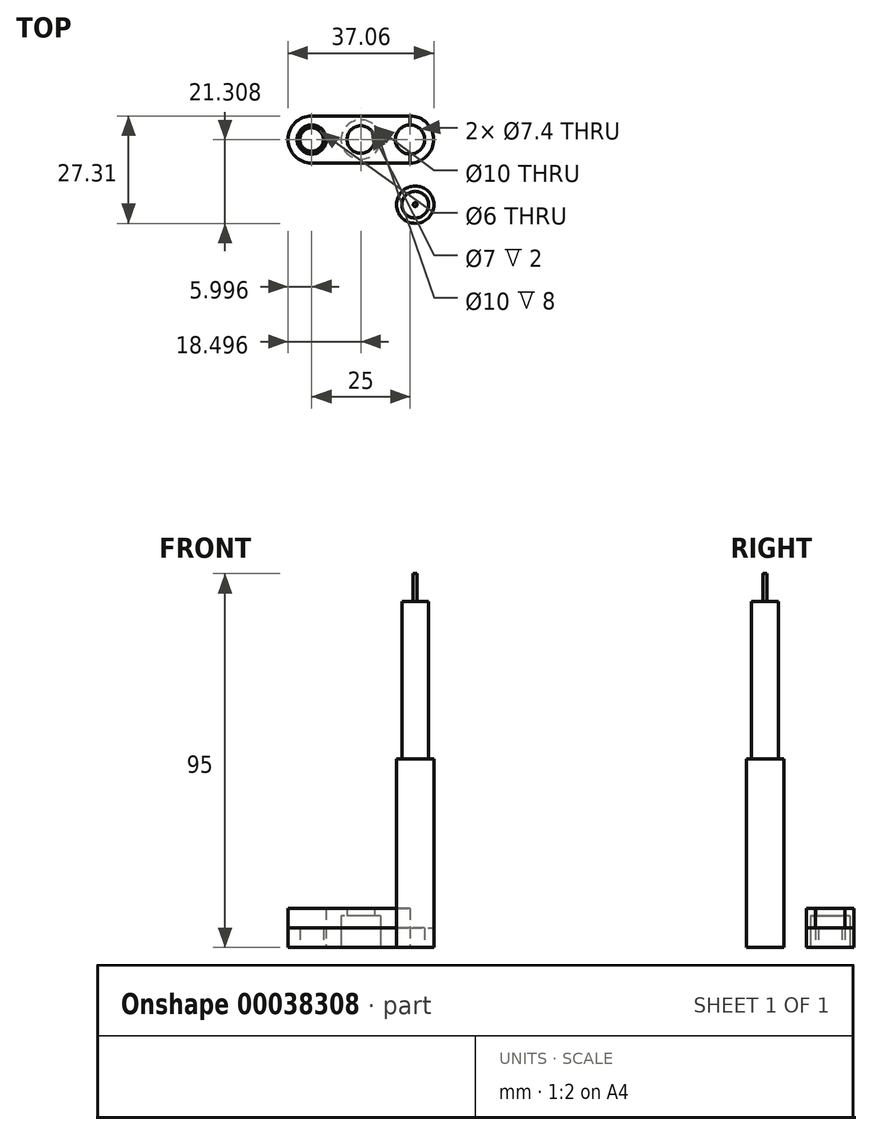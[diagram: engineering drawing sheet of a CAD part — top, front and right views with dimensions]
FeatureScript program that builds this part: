
annotation { "Feature Type Name" : "Feature", "Feature Type Description" : "" }
export const myFeature = defineFeature(function(context is Context, id is Id, definition is map)
    precondition{}
    {
        {
            var Q0;
            Q0=qCreatedBy(makeId("Top.planeOp"),FACE);
            var sketch = newSketch(context, id + "F0", { "sketchPlane" : qUnion([Q0])});
            skLineSegment(sketch, "E0.left", {"start": v(24.4, -16.97) * mm, "end": v(24.4, -4.97) * mm, "construction": true});
            skLineSegment(sketch, "E1", {"start": v(36.9, -4.97) * mm, "end": v(36.9, -16.97) * mm, "construction": true});
            skCircle(sketch, "E2", {"center": v(36.9, -10.97) * mm, "radius": 3.5 * mm});
            skArc(sketch, "E3", {"start": v(24.4, -4.97) * mm, "mid": v(18.4, -10.97) * mm, "end": v(24.4, -16.97) * mm});
            skCircle(sketch, "E4", {"center": v(24.4, -10.97) * mm, "radius": 3 * mm});
            skCircle(sketch, "E5", {"center": v(24.4, -10.97) * mm, "radius": 3.7 * mm});
            skCircle(sketch, "E6", {"center": v(36.9, -10.97) * mm, "radius": 5 * mm});
            skLineSegment(sketch, "E7", {"start": v(24.4, -4.97) * mm, "end": v(36.9, -4.97) * mm});
            skLineSegment(sketch, "E8", {"start": v(24.4, -16.97) * mm, "end": v(36.9, -16.97) * mm});
            skLineSegment(sketch, "E9.MirrorCS", {"start": v(49.4, -4.97) * mm, "end": v(36.9, -4.97) * mm});
            skLineSegment(sketch, "E10.MirrorCS", {"start": v(49.4, -16.97) * mm, "end": v(49.4, -4.97) * mm});
            skArc(sketch, "E11.MirrorCS", {"start": v(49.4, -4.97) * mm, "mid": v(55.4, -10.97) * mm, "end": v(49.4, -16.97) * mm});
            skLineSegment(sketch, "E12.MirrorCS", {"start": v(49.4, -16.97) * mm, "end": v(36.9, -16.97) * mm});
            skCircle(sketch, "E13.MirrorC", {"center": v(49.4, -10.97) * mm, "radius": 3.7 * mm});
            skCircle(sketch, "E14.MirrorC", {"center": v(49.4, -10.97) * mm, "radius": 3 * mm});
            skSolve(sketch);
        }
        {
            var Q0;
            Q0=qCreatedBy(makeId("Top.planeOp"),FACE);
            var sketch = newSketch(context, id + "F1", { "sketchPlane" : qUnion([Q0])});
            skCircle(sketch, "E15", {"center": v(50.71, -27.53) * mm, "radius": 4.75 * mm});
            skCircle(sketch, "E16", {"center": v(50.71, -27.53) * mm, "radius": 3.4 * mm});
            skCircle(sketch, "E17", {"center": v(50.71, -27.53) * mm, "radius": 0.5 * mm});
            skSolve(sketch);
        }
        {
            var Q0;
            Q0=makeQuery(id+"F1.imprint","IMPRINT",FACE,{"disambiguationData":[TD([[makeQuery(id+"F1.imprint","IMPRINT",EDGE,{"derivedFrom":sQuery(id+"F1.wireOp",EDGE,"E15")}),1.0]])]});
            var Q1;
            Q1=sQuery(id+"F1.wireOp",EDGE,"E15");
            extrude(context, id + "F2", {"entities" : qUnion([Q0]), "surfaceEntities" : qUnion([Q1]), "depth" : 48 * mm});
        }
        {
            var Q0;
            Q0=makeQuery(id+"F1.imprint","IMPRINT",FACE,{"disambiguationData":[TD([[makeQuery(id+"F1.imprint","IMPRINT",EDGE,{"derivedFrom":sQuery(id+"F1.wireOp",EDGE,"E16")}),1.0]])]});
            extrude(context, id + "F3", {"entities" : qUnion([Q0]), "operationType" : NewBodyOperationType.ADD, "depth" : 88 * mm});
        }
        {
            var Q0;
            Q0=makeQuery(id+"F1.imprint","IMPRINT",FACE,{"disambiguationData":[TD([[makeQuery(id+"F1.imprint","IMPRINT",EDGE,{"derivedFrom":sQuery(id+"F1.wireOp",EDGE,"E17")}),1.0]])]});
            extrude(context, id + "F4", {"entities" : qUnion([Q0]), "operationType" : NewBodyOperationType.ADD, "depth" : 95 * mm});
        }
        {
            var Q0;
            Q0=makeQuery(id+"F0.imprint","IMPRINT",FACE,{"disambiguationData":[TD([[makeQuery(id+"F0.imprint","IMPRINT",EDGE,{"derivedFrom":sQuery(id+"F0.wireOp",EDGE,"E4")}),-1.0]])]});
            var Q1;
            {var subQ1=sQuery(id+"F0.wireOp",EDGE,"E10.MirrorCS");var subQ4=sQuery(id+"F0.wireOp",EDGE,"E13.MirrorC");var subQ6=makeQuery(id+"F0.imprint","INTERSECT",VERTEX,{"disambiguationData":[OD(0.0)],"derivedFrom":[subQ1,subQ4]});Q1=makeQuery(id+"F0.imprint","IMPRINT",FACE,{"disambiguationData":[TD([[makeQuery(id+"F0.imprint","IMPRINT",EDGE,{"disambiguationData":[TD([[subQ6,-1.0]])],"derivedFrom":subQ1}),1.0]])]});}
            var Q2;
            {var subQ1=sQuery(id+"F0.wireOp",EDGE,"E10.MirrorCS");var subQ4=sQuery(id+"F0.wireOp",EDGE,"E13.MirrorC");var subQ6=makeQuery(id+"F0.imprint","INTERSECT",VERTEX,{"disambiguationData":[OD(0.0)],"derivedFrom":[subQ1,subQ4]});Q2=makeQuery(id+"F0.imprint","IMPRINT",FACE,{"disambiguationData":[TD([[makeQuery(id+"F0.imprint","IMPRINT",EDGE,{"disambiguationData":[TD([[subQ6,-1.0]])],"derivedFrom":subQ1}),-1.0]])]});}
            var Q3;
            Q3=sQuery(id+"F0.wireOp",EDGE,"E5");
            var Q4;
            Q4=sQuery(id+"F0.wireOp",EDGE,"E4");
            var Q5;
            Q5=sQuery(id+"F0.wireOp",EDGE,"E14.MirrorC");
            var Q6;
            Q6=sQuery(id+"F0.wireOp",EDGE,"E13.MirrorC");
            extrude(context, id + "F5", {"entities" : qUnion([Q0, Q1, Q2]), "surfaceEntities" : qUnion([Q3, Q4, Q5, Q6]), "depth" : 5 * mm});
        }
        {
            var Q0;
            Q0=makeQuery(id+"F0.imprint","IMPRINT",FACE,{"disambiguationData":[TD([[makeQuery(id+"F0.imprint","IMPRINT",EDGE,{"derivedFrom":sQuery(id+"F0.wireOp",EDGE,"E3")}),1.0]])]});
            var Q1;
            {var subQ4=sQuery(id+"F0.wireOp",EDGE,"E11.MirrorCS");Q1=makeQuery(id+"F0.imprint","IMPRINT",FACE,{"disambiguationData":[TD([[makeQuery(id+"F0.imprint","IMPRINT",EDGE,{"derivedFrom":subQ4}),-1.0]])]});}
            var Q2;
            Q2=makeQuery(id+"F0.imprint","IMPRINT",FACE,{"disambiguationData":[TD([[makeQuery(id+"F0.imprint","IMPRINT",EDGE,{"derivedFrom":sQuery(id+"F0.wireOp",EDGE,"E2")}),-1.0]])]});
            extrude(context, id + "F6", {"entities" : qUnion([Q0, Q1, Q2]), "depth" : 10 * mm});
        }
        {
            var Q0;
            Q0=makeQuery(id+"F0.imprint","IMPRINT",FACE,{"disambiguationData":[TD([[makeQuery(id+"F0.imprint","IMPRINT",EDGE,{"derivedFrom":sQuery(id+"F0.wireOp",EDGE,"E2")}),-1.0]])]});
            extrude(context, id + "F7", {"entities" : qUnion([Q0]), "operationType" : NewBodyOperationType.REMOVE, "depth" : 8 * mm});
        }
    });
